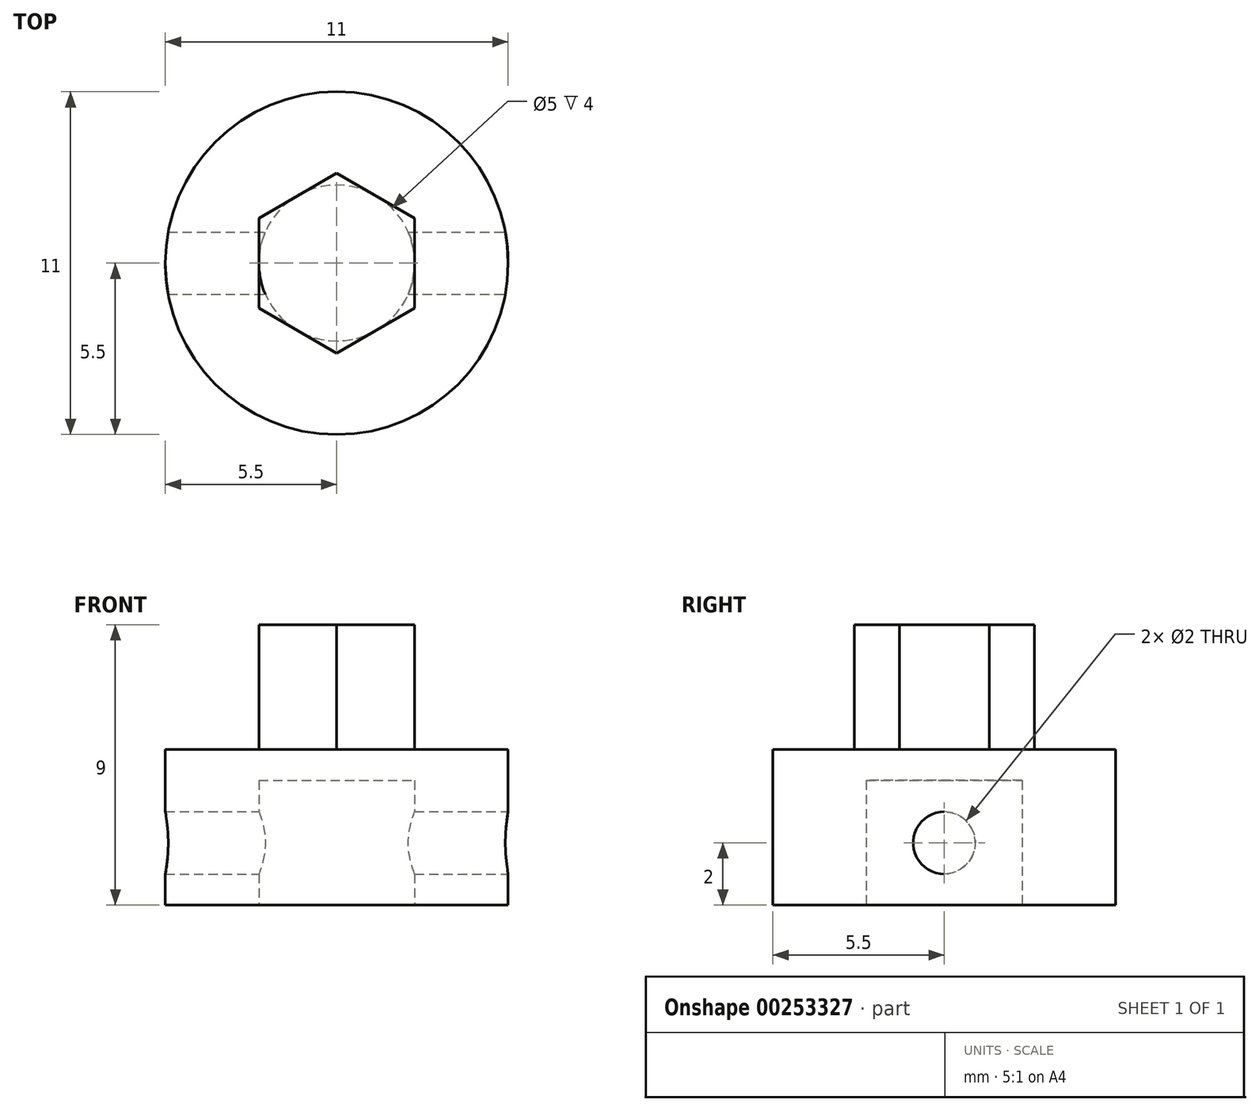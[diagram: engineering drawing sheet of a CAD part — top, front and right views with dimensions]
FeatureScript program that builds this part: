
annotation { "Feature Type Name" : "Feature", "Feature Type Description" : "" }
export const myFeature = defineFeature(function(context is Context, id is Id, definition is map)
    precondition{}
    {
        {
            var Q0;
            Q0=qCreatedBy(makeId("Top.planeOp"),FACE);
            var sketch = newSketch(context, id + "F0", { "sketchPlane" : qUnion([Q0])});
            skCircle(sketch, "E0", {"center": v(0, 0) * mm, "radius": 5.5 * mm});
            skCircle(sketch, "E1.cCircle", {"center": v(0, 0) * mm, "radius": 2.5 * mm, "construction": true});
            skLineSegment(sketch, "E1.0", {"start": v(-2.5, 1.44) * mm, "end": v(0, 2.89) * mm});
            skLineSegment(sketch, "E1.1", {"start": v(0, 2.89) * mm, "end": v(2.5, 1.44) * mm});
            skLineSegment(sketch, "E1.2", {"start": v(2.5, 1.44) * mm, "end": v(2.5, -1.44) * mm});
            skLineSegment(sketch, "E1.3", {"start": v(2.5, -1.44) * mm, "end": v(0, -2.89) * mm});
            skLineSegment(sketch, "E1.4", {"start": v(0, -2.89) * mm, "end": v(-2.5, -1.44) * mm});
            skLineSegment(sketch, "E1.5", {"start": v(-2.5, -1.44) * mm, "end": v(-2.5, 1.44) * mm});
            skPoint(sketch, "E1.0.midPoint", {"position": v(-1.25, 2.17) * mm});
            skSolve(sketch);
        }
        {
            var Q0;
            Q0=makeQuery(id+"F0.imprint","IMPRINT",FACE,{"disambiguationData":[TD([[makeQuery(id+"F0.imprint","IMPRINT",EDGE,{"derivedFrom":sQuery(id+"F0.wireOp",EDGE,"E1.0")}),-1.0]])]});
            extrude(context, id + "F1", {"entities" : qUnion([Q0]), "depth" : 9 * mm});
        }
        {
            var Q0;
            Q0=makeQuery(id+"F0.imprint","IMPRINT",FACE,{"disambiguationData":[TD([[makeQuery(id+"F0.imprint","IMPRINT",EDGE,{"derivedFrom":sQuery(id+"F0.wireOp",EDGE,"E0")}),1.0]])]});
            extrude(context, id + "F2", {"entities" : qUnion([Q0]), "operationType" : NewBodyOperationType.ADD, "depth" : 5 * mm});
        }
        {
            var Q0;
            Q0=qCreatedBy(makeId("Right.planeOp"),FACE);
            var sketch = newSketch(context, id + "F3", { "sketchPlane" : qUnion([Q0])});
            skLineSegment(sketch, "E2.bottom", {"start": v(-2.5, 4) * mm, "end": v(2.5, 4) * mm});
            skLineSegment(sketch, "E2.top", {"start": v(-2.5, -4) * mm, "end": v(2.5, -4) * mm});
            skLineSegment(sketch, "E2.left", {"start": v(-2.5, 4) * mm, "end": v(-2.5, -4) * mm, "construction": true});
            skLineSegment(sketch, "E2.right", {"start": v(2.5, 4) * mm, "end": v(2.5, -4) * mm});
            skPoint(sketch, "E2.middle", {"position": v(0, 0) * mm});
            skCircle(sketch, "E3", {"center": v(0, 2) * mm, "radius": 1 * mm, "construction": true});
            skLineSegment(sketch, "E4", {"start": v(0, 4.73) * mm, "end": v(0, -5.32) * mm});
            skSolve(sketch);
        }
        {
            var Q0;
            {var subQ0=sQuery(id+"F3.wireOp",EDGE,"E2.right");Q0=makeQuery(id+"F3.imprint","IMPRINT",FACE,{"disambiguationData":[TD([[makeQuery(id+"F3.imprint","IMPRINT",EDGE,{"derivedFrom":subQ0}),-1.0]])]});}
            var Q1;
            Q1 = qConstructionFilter(qBodyType(qCreatedBy(id + "F3" ,EDGE), BodyType.WIRE), ConstructionObject.NO);
            var Q2;
            Q2=sQuery(id+"F3.wireOp",EDGE,"E4");
            revolve(context, id + "F4", {"operationType" : NewBodyOperationType.REMOVE, "entities" : qUnion([Q0]), "surfaceEntities" : qUnion([Q1]), "axis" : qUnion([Q2]), "revolveType" : RevolveType.FULL, "oppositeDirection" : true});
        }
        {
            var Q0;
            Q0=qCreatedBy(makeId("Right.planeOp"),FACE);
            var sketch = newSketch(context, id + "F5", { "sketchPlane" : qUnion([Q0])});
            skCircle(sketch, "E5.0", {"center": v(0, 2) * mm, "radius": 1 * mm});
            skSolve(sketch);
        }
        {
            var Q0;
            Q0 = qSketchRegion(id + "F5", true);
            extrude(context, id + "F6", {"entities" : qUnion([Q0]), "operationType" : NewBodyOperationType.REMOVE, "endBound" : BoundingType.SYMMETRIC, "oppositeDirection" : true, "depth" : 25 * mm});
        }
    });
